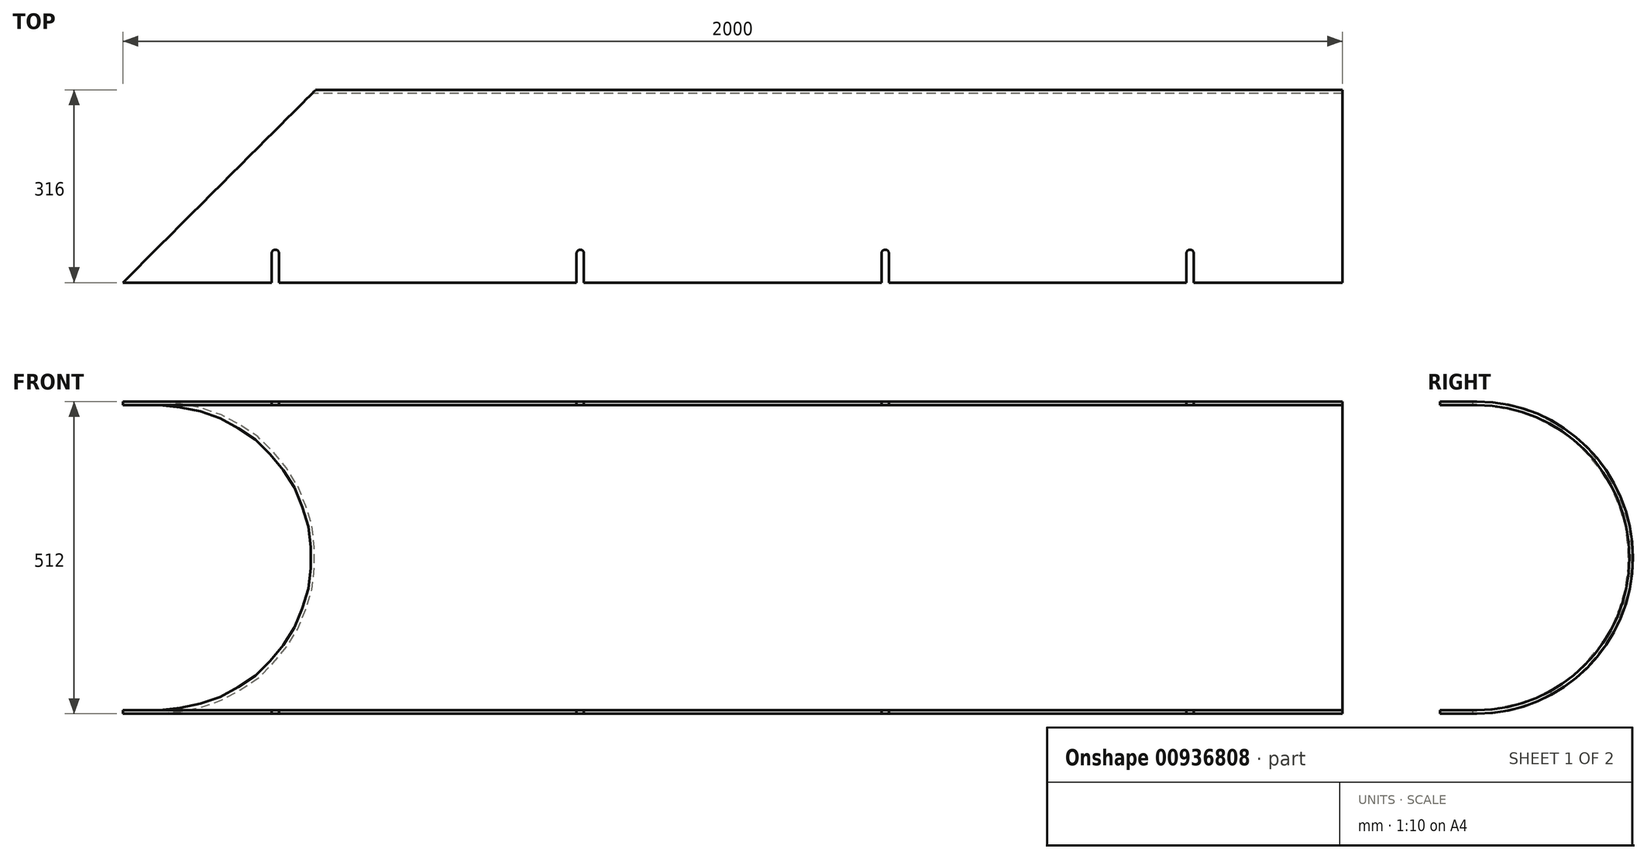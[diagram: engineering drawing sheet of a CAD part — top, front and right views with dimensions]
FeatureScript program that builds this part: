
annotation { "Feature Type Name" : "Feature", "Feature Type Description" : "" }
export const myFeature = defineFeature(function(context is Context, id is Id, definition is map)
    precondition{}
    {
        {
            var Q0;
            Q0=qCreatedBy(makeId("Right.planeOp"),FACE);
            var sketch = newSketch(context, id + "F0", { "sketchPlane" : qUnion([Q0])});
            skArc(sketch, "E0", {"start": v(0, -250) * mm, "mid": v(250, 0) * mm, "end": v(0, 250) * mm});
            skArc(sketch, "E1", {"start": v(0, -256) * mm, "mid": v(256, 0) * mm, "end": v(0, 256) * mm});
            skLineSegment(sketch, "E2", {"start": v(0, 256) * mm, "end": v(-60, 256) * mm});
            skLineSegment(sketch, "E3", {"start": v(-60, 256) * mm, "end": v(-60, 250) * mm});
            skLineSegment(sketch, "E4", {"start": v(-60, 250) * mm, "end": v(0, 250) * mm});
            skLineSegment(sketch, "E5", {"start": v(0, -256) * mm, "end": v(-60, -256) * mm});
            skLineSegment(sketch, "E6", {"start": v(-60, -256) * mm, "end": v(-60, -250) * mm});
            skLineSegment(sketch, "E7", {"start": v(-60, -250) * mm, "end": v(0, -250) * mm});
            skSolve(sketch);
        }
        {
            var Q0;
            Q0=makeQuery(id+"F0.imprint","IMPRINT",FACE,{"disambiguationData":[TD([[makeQuery(id+"F0.imprint","IMPRINT",EDGE,{"derivedFrom":sQuery(id+"F0.wireOp",EDGE,"E0")}),-1.0]])]});
            extrude(context, id + "F1", {"entities" : qUnion([Q0]), "depth" : 2000 * mm, "offsetDistance" : 25 * mm});
        }
        {
            var Q0;
            Q0=makeQuery(id+"F1.opExtrude","SWEPT_FACE",FACE,{"disambiguationData":[OSD([sQuery(id+"F0.wireOp",EDGE,"E2")])]});
            var sketch = newSketch(context, id + "F2", { "sketchPlane" : qUnion([Q0])});
            skPoint(sketch, "E8.0", {"position": v(0, -60) * mm});
            skLineSegment(sketch, "E9", {"start": v(0, -60) * mm, "end": v(316, 256) * mm});
            skLineSegment(sketch, "E10", {"start": v(0, 256) * mm, "end": v(316, 256) * mm});
            skLineSegment(sketch, "E11", {"start": v(0, 256) * mm, "end": v(0, -60) * mm});
            skSolve(sketch);
        }
        {
            var Q0;
            {var subQ0=sQuery(id+"F2.wireOp",EDGE,"E10");Q0=makeQuery(id+"F2.imprint","IMPRINT",FACE,{"disambiguationData":[TD([[makeQuery(id+"F2.imprint","IMPRINT",EDGE,{"derivedFrom":subQ0}),-1.0]])]});}
            var Q1;
            {var subQ1=sQuery(id+"F2.wireOp",EDGE,"E9");var subQ2=sQuery(id+"F0.wireOp",EDGE,"E2");var subQ4=makeQuery(id+"F1.opExtrude","SWEPT_EDGE",EDGE,{"disambiguationData":[OSD([sQuery(id+"F0.wireOp",EDGE,"E1"),subQ2])]});var subQ5=makeQuery(id+"F2.imprint","INTERSECT",VERTEX,{"derivedFrom":[subQ4,subQ1]});Q1=makeQuery(id+"F2.imprint","IMPRINT",FACE,{"disambiguationData":[TD([[makeQuery(id+"F2.imprint","IMPRINT",EDGE,{"disambiguationData":[TD([[subQ5,1.0]])],"derivedFrom":subQ1}),1.0]])]});}
            extrude(context, id + "F3", {"entities" : qUnion([Q0, Q1]), "operationType" : NewBodyOperationType.REMOVE, "oppositeDirection" : true, "depth" : 550 * mm, "offsetDistance" : 25 * mm});
        }
        {
            var Q0;
            Q0=makeQuery(id+"F1.opExtrude","SWEPT_FACE",FACE,{"disambiguationData":[OSD([sQuery(id+"F0.wireOp",EDGE,"E2")])]});
            var sketch = newSketch(context, id + "F4", { "sketchPlane" : qUnion([Q0])});
            skLineSegment(sketch, "E12", {"start": v(244, -60) * mm, "end": v(244, -12) * mm});
            skLineSegment(sketch, "E13.0", {"start": v(256, -60) * mm, "end": v(256, -12) * mm});
            skArc(sketch, "E14", {"start": v(256, -12) * mm, "mid": v(250, -6) * mm, "end": v(244, -12) * mm});
            skLineSegment(sketch, "E15", {"start": v(244, -60) * mm, "end": v(256, -60) * mm});
            skLineSegment(sketch, "E16.1.0.0", {"start": v(744, -60) * mm, "end": v(756, -60) * mm});
            skLineSegment(sketch, "E16.1.0.1", {"start": v(744, -60) * mm, "end": v(744, -12) * mm});
            skLineSegment(sketch, "E16.1.0.2", {"start": v(756, -60) * mm, "end": v(756, -12) * mm});
            skArc(sketch, "E16.1.0.3", {"start": v(756, -12) * mm, "mid": v(750, -6) * mm, "end": v(744, -12) * mm});
            skLineSegment(sketch, "E16.2.0.0", {"start": v(1244, -60) * mm, "end": v(1256, -60) * mm});
            skLineSegment(sketch, "E16.2.0.1", {"start": v(1244, -60) * mm, "end": v(1244, -12) * mm});
            skLineSegment(sketch, "E16.2.0.2", {"start": v(1256, -60) * mm, "end": v(1256, -12) * mm});
            skArc(sketch, "E16.2.0.3", {"start": v(1256, -12) * mm, "mid": v(1250, -6) * mm, "end": v(1244, -12) * mm});
            skLineSegment(sketch, "E16.3.0.0", {"start": v(1744, -60) * mm, "end": v(1756, -60) * mm});
            skLineSegment(sketch, "E16.3.0.1", {"start": v(1744, -60) * mm, "end": v(1744, -12) * mm});
            skLineSegment(sketch, "E16.3.0.2", {"start": v(1756, -60) * mm, "end": v(1756, -12) * mm});
            skArc(sketch, "E16.3.0.3", {"start": v(1756, -12) * mm, "mid": v(1750, -6) * mm, "end": v(1744, -12) * mm});
            skLineSegment(sketch, "E16.direction1", {"start": v(244, -60) * mm, "end": v(744, -60) * mm, "construction": true});
            skSolve(sketch);
        }
        {
            var Q0;
            Q0=makeQuery(id+"F4.imprint","IMPRINT",FACE,{"disambiguationData":[TD([[makeQuery(id+"F4.imprint","IMPRINT",EDGE,{"derivedFrom":sQuery(id+"F4.wireOp",EDGE,"E12")}),-1.0]])]});
            var Q1;
            Q1=makeQuery(id+"F4.imprint","IMPRINT",FACE,{"disambiguationData":[TD([[makeQuery(id+"F4.imprint","IMPRINT",EDGE,{"derivedFrom":sQuery(id+"F4.wireOp",EDGE,"E16.1.0.0")}),-1.0]])]});
            var Q2;
            Q2=makeQuery(id+"F4.imprint","IMPRINT",FACE,{"disambiguationData":[TD([[makeQuery(id+"F4.imprint","IMPRINT",EDGE,{"derivedFrom":sQuery(id+"F4.wireOp",EDGE,"E16.2.0.0")}),-1.0]])]});
            var Q3;
            Q3=makeQuery(id+"F4.imprint","IMPRINT",FACE,{"disambiguationData":[TD([[makeQuery(id+"F4.imprint","IMPRINT",EDGE,{"derivedFrom":sQuery(id+"F4.wireOp",EDGE,"E16.3.0.0")}),-1.0]])]});
            extrude(context, id + "F5", {"entities" : qUnion([Q0, Q1, Q2, Q3]), "operationType" : NewBodyOperationType.REMOVE, "endBound" : BoundingType.THROUGH_ALL, "oppositeDirection" : true, "depth" : 25 * mm, "offsetDistance" : 25 * mm});
        }
    });
